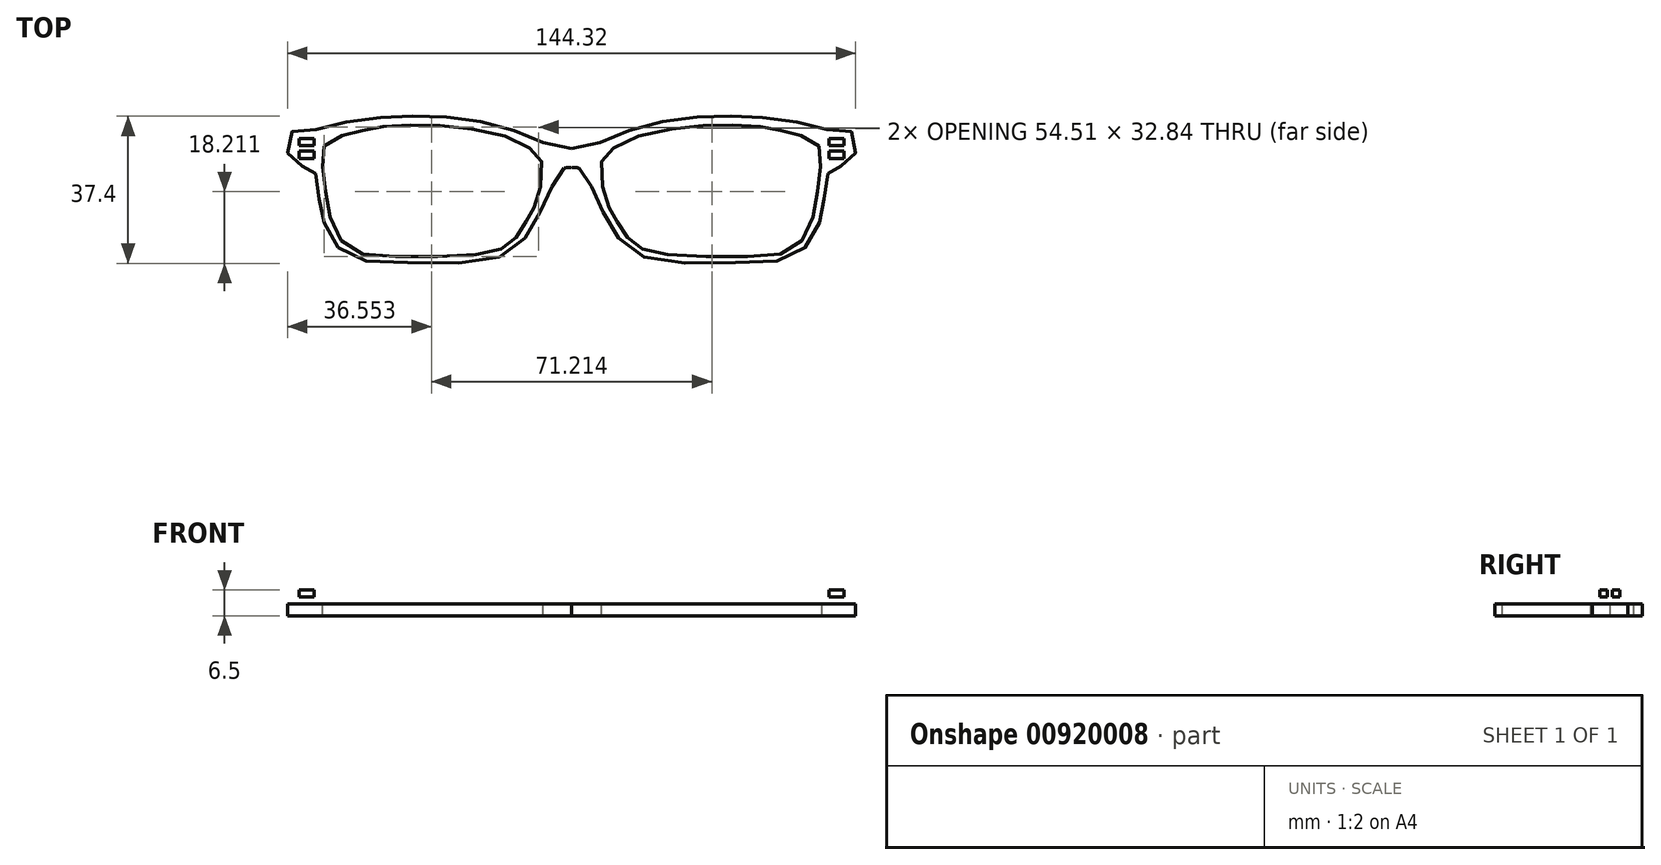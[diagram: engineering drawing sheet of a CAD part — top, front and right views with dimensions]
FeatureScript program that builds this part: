
annotation { "Feature Type Name" : "Feature", "Feature Type Description" : "" }
export const myFeature = defineFeature(function(context is Context, id is Id, definition is map)
    precondition{}
    {
        {
            var Q0;
            Q0=qCreatedBy(makeId("Top.planeOp"),FACE);
            var sketch = newSketch(context, id + "F0", { "sketchPlane" : qUnion([Q0])});
            skFitSpline(sketch, "E0", {"points": [v(-71.2, -2.06) * mm, v(-66.62, -1.6) * mm, v(-59.06, 0.05) * mm, v(-48.74, 1.6) * mm, v(-39.71, 1.97) * mm, v(-29.36, 1.55) * mm, v(-19.11, -0.24) * mm, v(-9.67, -3.58) * mm, v(-2.94, -6.1) * mm, v(3.4, -7.2) * mm, v(2.95, -10.9) * mm, v(-1.05, -11.09) * mm, v(-3.42, -12.64) * mm, v(-6.1, -18.5) * mm, v(-9.16, -24.56) * mm, v(-14.22, -31.57) * mm, v(-24.62, -35.13) * mm, v(-45.9, -35.12) * mm, v(-56.62, -33.56) * mm, v(-62.09, -27.3) * mm, v(-63.57, -22.11) * mm, v(-64.54, -16.87) * mm, v(-65.27, -11.73) * mm, v(-66.04, -10.74) * mm, v(-71.4, -10.24) * mm, v(-71.96, -5.63) * mm, v(-71.2, -2.06) * mm]});
            skFitSpline(sketch, "E1", {"points": [v(-62.86, -5.55) * mm, v(-58.46, -3) * mm, v(-53.38, -1.76) * mm, v(-48.23, -0.74) * mm, v(-38.98, -0.26) * mm, v(-27.96, -0.94) * mm, v(-15, -3.8) * mm, v(-9, -7.46) * mm, v(-7.46, -10.49) * mm, v(-8.58, -18.79) * mm, v(-10.01, -22.15) * mm, v(-11.7, -25.05) * mm, v(-14.06, -28.75) * mm, v(-17.33, -31.51) * mm, v(-24.57, -33.23) * mm, v(-44.14, -33.65) * mm, v(-55.75, -32.1) * mm, v(-60.55, -25.98) * mm, v(-62.35, -18.13) * mm, v(-63.23, -10.61) * mm, v(-62.86, -5.55) * mm]});
            skLineSegment(sketch, "E2", {"start": v(0, 10.33) * mm, "end": v(0, -43.44) * mm});
            skFitSpline(sketch, "E3.MirrorC", {"points": [v(71.2, -2.06) * mm, v(66.62, -1.6) * mm, v(59.06, 0.05) * mm, v(48.74, 1.6) * mm, v(39.71, 1.97) * mm, v(29.36, 1.55) * mm, v(19.11, -0.24) * mm, v(9.67, -3.58) * mm, v(2.94, -6.1) * mm, v(-3.4, -7.2) * mm, v(-2.95, -10.9) * mm, v(1.05, -11.09) * mm, v(3.42, -12.64) * mm, v(6.1, -18.5) * mm, v(9.16, -24.56) * mm, v(14.22, -31.57) * mm, v(24.62, -35.13) * mm, v(45.9, -35.12) * mm, v(56.62, -33.56) * mm, v(62.09, -27.3) * mm, v(63.57, -22.11) * mm, v(64.54, -16.87) * mm, v(65.27, -11.73) * mm, v(66.04, -10.74) * mm, v(71.4, -10.24) * mm, v(71.96, -5.63) * mm, v(71.2, -2.06) * mm]});
            skFitSpline(sketch, "E4.MirrorC", {"points": [v(62.86, -5.55) * mm, v(58.46, -3) * mm, v(53.38, -1.76) * mm, v(48.23, -0.74) * mm, v(38.98, -0.26) * mm, v(27.96, -0.94) * mm, v(15, -3.8) * mm, v(9, -7.46) * mm, v(7.46, -10.49) * mm, v(8.58, -18.79) * mm, v(10.01, -22.15) * mm, v(11.7, -25.05) * mm, v(14.06, -28.75) * mm, v(17.33, -31.51) * mm, v(24.57, -33.23) * mm, v(44.14, -33.65) * mm, v(55.75, -32.1) * mm, v(60.55, -25.98) * mm, v(62.35, -18.13) * mm, v(63.23, -10.61) * mm, v(62.86, -5.55) * mm]});
            skSolve(sketch);
        }
        {
            var Q0;
            Q0=makeQuery(id+"F0.imprint","IMPRINT",FACE,{"disambiguationData":[TD([[makeQuery(id+"F0.imprint","IMPRINT",EDGE,{"derivedFrom":sQuery(id+"F0.wireOp",EDGE,"E1")}),1.0]])]});
            var Q1;
            {var subQ0=sQuery(id+"F0.wireOp",EDGE,"E3.MirrorC");var subQ1=sQuery(id+"F0.wireOp",EDGE,"E0");var subQ2=makeQuery(id+"F0.imprint","INTERSECT",VERTEX,{"disambiguationData":[OD(1.0)],"derivedFrom":[subQ1,subQ0]});Q1=makeQuery(id+"F0.imprint","IMPRINT",FACE,{"disambiguationData":[TD([[makeQuery(id+"F0.imprint","IMPRINT",EDGE,{"disambiguationData":[TD([[subQ2,1.0]])],"derivedFrom":subQ1}),-1.0]])]});}
            var Q2;
            {var subQ0=sQuery(id+"F0.wireOp",EDGE,"E3.MirrorC");var subQ1=sQuery(id+"F0.wireOp",EDGE,"E0");var subQ2=makeQuery(id+"F0.imprint","INTERSECT",VERTEX,{"disambiguationData":[OD(0.0)],"derivedFrom":[subQ1,subQ0]});Q2=makeQuery(id+"F0.imprint","IMPRINT",FACE,{"disambiguationData":[TD([[makeQuery(id+"F0.imprint","IMPRINT",EDGE,{"disambiguationData":[TD([[subQ2,1.0]])],"derivedFrom":subQ1}),-1.0]])]});}
            var Q3;
            Q3=makeQuery(id+"F0.imprint","IMPRINT",FACE,{"disambiguationData":[TD([[makeQuery(id+"F0.imprint","IMPRINT",EDGE,{"derivedFrom":sQuery(id+"F0.wireOp",EDGE,"E4.MirrorC")}),-1.0]])]});
            extrude(context, id + "F1", {"entities" : qUnion([Q0, Q1, Q2, Q3]), "depth" : 3 * mm, "offsetDistance" : 25 * mm});
        }
        {
            var Q0;
            Q0=makeQuery(id+"F1.opExtrude","CAP_FACE",FACE,{"disambiguationData":[OSD([sQuery(id+"F0.wireOp",EDGE,"E0"),sQuery(id+"F0.wireOp",EDGE,"E1"),sQuery(id+"F0.wireOp",EDGE,"9bc1a8fa-3d3e-4df0-bdc8-d42c7dd6f2910.MirrorC"),sQuery(id+"F0.wireOp",EDGE,"305769e5-fb78-4a35-a487-b496d2b2eac20.MirrorC")])],"isStart":false});
            var sketch = newSketch(context, id + "F2", { "sketchPlane" : qUnion([Q0])});
            skLineSegment(sketch, "E5", {"start": v(-72.2, -10.82) * mm, "end": v(-72.2, -3.27) * mm});
            skLineSegment(sketch, "E6.bottom", {"start": v(-69.2, -3.75) * mm, "end": v(-65.4, -3.75) * mm});
            skLineSegment(sketch, "E6.top", {"start": v(-69.2, -8.75) * mm, "end": v(-65.4, -8.75) * mm});
            skLineSegment(sketch, "E6.left", {"start": v(-69.2, -3.75) * mm, "end": v(-69.2, -8.75) * mm});
            skLineSegment(sketch, "E6.right", {"start": v(-65.4, -3.75) * mm, "end": v(-65.4, -8.75) * mm});
            skPoint(sketch, "E6.middle", {"position": v(-67.3, -6.25) * mm});
            skLineSegment(sketch, "E7.MirrorCS", {"start": v(69.2, -3.75) * mm, "end": v(65.4, -3.75) * mm});
            skLineSegment(sketch, "E8.MirrorCS", {"start": v(69.2, -3.75) * mm, "end": v(69.2, -8.75) * mm});
            skLineSegment(sketch, "E9.MirrorCS", {"start": v(65.4, -3.75) * mm, "end": v(65.4, -8.75) * mm});
            skLineSegment(sketch, "E10.MirrorCS", {"start": v(69.2, -8.75) * mm, "end": v(65.4, -8.75) * mm});
            skSolve(sketch);
        }
        {
            var Q0;
            Q0=makeQuery(id+"F2.imprint","IMPRINT",FACE,{"disambiguationData":[TD([[makeQuery(id+"F2.imprint","IMPRINT",EDGE,{"derivedFrom":sQuery(id+"F2.wireOp",EDGE,"E6.bottom")}),-1.0]])]});
            var Q1;
            Q1=makeQuery(id+"F2.imprint","IMPRINT",FACE,{"disambiguationData":[TD([[makeQuery(id+"F2.imprint","IMPRINT",EDGE,{"derivedFrom":sQuery(id+"F2.wireOp",EDGE,"E7.MirrorCS")}),1.0]])]});
            extrude(context, id + "F3", {"entities" : qUnion([Q0, Q1]), "operationType" : NewBodyOperationType.ADD, "depth" : 3.5 * mm, "offsetDistance" : 25 * mm});
        }
        {
            var Q0;
            Q0=makeQuery(id+"F3.opExtrude","SWEPT_FACE",FACE,{"disambiguationData":[OSD([sQuery(id+"F2.wireOp",EDGE,"E8.MirrorCS")])]});
            var sketch = newSketch(context, id + "F4", { "sketchPlane" : qUnion([Q0])});
            skLineSegment(sketch, "E11.bottom", {"start": v(-6.9, 6.5) * mm, "end": v(-5.55, 6.5) * mm});
            skLineSegment(sketch, "E11.top", {"start": v(-6.9, 3) * mm, "end": v(-5.55, 3) * mm});
            skPoint(sketch, "E11.middle", {"position": v(-6.22, 4.75) * mm});
            skLineSegment(sketch, "E12", {"start": v(-6.9, 6.5) * mm, "end": v(-6.9, 3) * mm});
            skLineSegment(sketch, "E13", {"start": v(-5.55, 6.5) * mm, "end": v(-5.55, 3) * mm});
            skSolve(sketch);
        }
        {
            var Q0;
            Q0=makeQuery(id+"F3.opExtrude","SWEPT_FACE",FACE,{"disambiguationData":[OSD([sQuery(id+"F2.wireOp",EDGE,"E6.left")])]});
            var sketch = newSketch(context, id + "F5", { "sketchPlane" : qUnion([Q0])});
            skLineSegment(sketch, "E14.bottom", {"start": v(5.55, 6.5) * mm, "end": v(6.9, 6.5) * mm});
            skLineSegment(sketch, "E14.top", {"start": v(5.55, 3) * mm, "end": v(6.9, 3) * mm});
            skLineSegment(sketch, "E14.left", {"start": v(5.55, 6.5) * mm, "end": v(5.55, 3) * mm});
            skLineSegment(sketch, "E14.right", {"start": v(6.9, 6.5) * mm, "end": v(6.9, 3) * mm});
            skSolve(sketch);
        }
        {
            var Q0;
            Q0=makeQuery(id+"F5.imprint","IMPRINT",FACE,{"disambiguationData":[TD([[makeQuery(id+"F5.imprint","IMPRINT",EDGE,{"derivedFrom":sQuery(id+"F5.wireOp",EDGE,"E14.bottom")}),-1.0]])]});
            extrude(context, id + "F6", {"entities" : qUnion([Q0]), "operationType" : NewBodyOperationType.REMOVE, "oppositeDirection" : true, "depth" : 5 * mm, "offsetDistance" : 25 * mm});
        }
        {
            var Q0;
            Q0=makeQuery(id+"F4.imprint","IMPRINT",FACE,{"disambiguationData":[TD([[makeQuery(id+"F4.imprint","IMPRINT",EDGE,{"derivedFrom":sQuery(id+"F4.wireOp",EDGE,"E11.bottom")}),1.0]])]});
            extrude(context, id + "F7", {"entities" : qUnion([Q0]), "operationType" : NewBodyOperationType.REMOVE, "oppositeDirection" : true, "depth" : 5 * mm, "offsetDistance" : 25 * mm});
        }
        {
            var Q0;
            Q0=makeQuery(id+"F3.opExtrude","SWEPT_FACE",FACE,{"disambiguationData":[OSD([sQuery(id+"F2.wireOp",EDGE,"E6.bottom")])]});
            var sketch = newSketch(context, id + "F8", { "sketchPlane" : qUnion([Q0])});
            skPoint(sketch, "E15", {"position": v(67.3, 6.5) * mm});
            skLineSegment(sketch, "E16", {"start": v(67.3, 6.5) * mm, "end": v(67.3, 3) * mm});
            skLineSegment(sketch, "E17", {"start": v(65.4, 4.75) * mm, "end": v(69.2, 4.75) * mm});
            skCircle(sketch, "E18", {"center": v(67.3, 4.75) * mm, "radius": 0.55 * mm});
            skSolve(sketch);
        }
        {
            var Q0;
            Q0=makeQuery(id+"F3.opExtrude","SWEPT_FACE",FACE,{"disambiguationData":[OSD([sQuery(id+"F2.wireOp",EDGE,"E7.MirrorCS")])]});
            var sketch = newSketch(context, id + "F9", { "sketchPlane" : qUnion([Q0])});
            skLineSegment(sketch, "E19", {"start": v(-67.3, 6.5) * mm, "end": v(-67.3, 3) * mm});
            skLineSegment(sketch, "E20", {"start": v(-69.2, 4.75) * mm, "end": v(-65.4, 4.75) * mm});
            skCircle(sketch, "E21", {"center": v(-67.3, 4.75) * mm, "radius": 0.55 * mm});
            skSolve(sketch);
        }
        {
            var Q0;
            {var subQ0=sQuery(id+"F9.wireOp",EDGE,"E20");var subQ1=sQuery(id+"F9.wireOp",EDGE,"E19");var subQ2=makeQuery(id+"F9.imprint","INTERSECT",VERTEX,{"derivedFrom":[subQ1,subQ0]});Q0=makeQuery(id+"F9.imprint","IMPRINT",FACE,{"disambiguationData":[TD([[makeQuery(id+"F9.imprint","IMPRINT",EDGE,{"disambiguationData":[TD([[subQ2,-1.0]])],"derivedFrom":subQ1}),1.0]])]});}
            var Q1;
            {var subQ0=sQuery(id+"F9.wireOp",EDGE,"E21");var subQ1=sQuery(id+"F9.wireOp",EDGE,"E19");var subQ2=makeQuery(id+"F9.imprint","INTERSECT",VERTEX,{"disambiguationData":[OD(0.0)],"derivedFrom":[subQ1,subQ0]});Q1=makeQuery(id+"F9.imprint","IMPRINT",FACE,{"disambiguationData":[TD([[makeQuery(id+"F9.imprint","IMPRINT",EDGE,{"disambiguationData":[TD([[subQ2,-1.0]])],"derivedFrom":subQ1}),1.0]])]});}
            var Q2;
            {var subQ0=sQuery(id+"F9.wireOp",EDGE,"E21");var subQ1=sQuery(id+"F9.wireOp",EDGE,"E19");var subQ2=makeQuery(id+"F9.imprint","INTERSECT",VERTEX,{"disambiguationData":[OD(0.0)],"derivedFrom":[subQ1,subQ0]});Q2=makeQuery(id+"F9.imprint","IMPRINT",FACE,{"disambiguationData":[TD([[makeQuery(id+"F9.imprint","IMPRINT",EDGE,{"disambiguationData":[TD([[subQ2,-1.0]])],"derivedFrom":subQ1}),-1.0]])]});}
            var Q3;
            {var subQ0=sQuery(id+"F9.wireOp",EDGE,"E20");var subQ1=sQuery(id+"F9.wireOp",EDGE,"E19");var subQ2=makeQuery(id+"F9.imprint","INTERSECT",VERTEX,{"derivedFrom":[subQ1,subQ0]});Q3=makeQuery(id+"F9.imprint","IMPRINT",FACE,{"disambiguationData":[TD([[makeQuery(id+"F9.imprint","IMPRINT",EDGE,{"disambiguationData":[TD([[subQ2,-1.0]])],"derivedFrom":subQ1}),-1.0]])]});}
            var Q4;
            {var subQ0=sQuery(id+"F8.wireOp",EDGE,"E17");var subQ1=sQuery(id+"F8.wireOp",EDGE,"E16");var subQ2=makeQuery(id+"F8.imprint","INTERSECT",VERTEX,{"derivedFrom":[subQ1,subQ0]});Q4=makeQuery(id+"F8.imprint","IMPRINT",FACE,{"disambiguationData":[TD([[makeQuery(id+"F8.imprint","IMPRINT",EDGE,{"disambiguationData":[TD([[subQ2,-1.0]])],"derivedFrom":subQ1}),1.0]])]});}
            var Q5;
            {var subQ0=sQuery(id+"F8.wireOp",EDGE,"E18");var subQ1=sQuery(id+"F8.wireOp",EDGE,"E16");var subQ2=makeQuery(id+"F8.imprint","INTERSECT",VERTEX,{"disambiguationData":[OD(0.0)],"derivedFrom":[subQ1,subQ0]});Q5=makeQuery(id+"F8.imprint","IMPRINT",FACE,{"disambiguationData":[TD([[makeQuery(id+"F8.imprint","IMPRINT",EDGE,{"disambiguationData":[TD([[subQ2,-1.0]])],"derivedFrom":subQ1}),1.0]])]});}
            var Q6;
            {var subQ0=sQuery(id+"F8.wireOp",EDGE,"E18");var subQ1=sQuery(id+"F8.wireOp",EDGE,"E16");var subQ2=makeQuery(id+"F8.imprint","INTERSECT",VERTEX,{"disambiguationData":[OD(0.0)],"derivedFrom":[subQ1,subQ0]});Q6=makeQuery(id+"F8.imprint","IMPRINT",FACE,{"disambiguationData":[TD([[makeQuery(id+"F8.imprint","IMPRINT",EDGE,{"disambiguationData":[TD([[subQ2,-1.0]])],"derivedFrom":subQ1}),-1.0]])]});}
            var Q7;
            {var subQ0=sQuery(id+"F8.wireOp",EDGE,"E17");var subQ1=sQuery(id+"F8.wireOp",EDGE,"E16");var subQ2=makeQuery(id+"F8.imprint","INTERSECT",VERTEX,{"derivedFrom":[subQ1,subQ0]});Q7=makeQuery(id+"F8.imprint","IMPRINT",FACE,{"disambiguationData":[TD([[makeQuery(id+"F8.imprint","IMPRINT",EDGE,{"disambiguationData":[TD([[subQ2,-1.0]])],"derivedFrom":subQ1}),-1.0]])]});}
            extrude(context, id + "F10", {"entities" : qUnion([Q0, Q1, Q2, Q3, Q4, Q5, Q6, Q7]), "operationType" : NewBodyOperationType.REMOVE, "oppositeDirection" : true, "depth" : 6 * mm, "offsetDistance" : 25 * mm});
        }
    });
